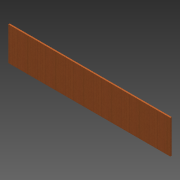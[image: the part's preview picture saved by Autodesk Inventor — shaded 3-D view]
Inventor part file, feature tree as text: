
AUTODESK INVENTOR PART (.ipt)
format: ipt  version: 2013 (Build 170138000, 138)  size: 80,896 bytes
history: native  units: in
note: dims shown in document units (in); Inventor stores cm internally (conversion verified against a paired STEP export)
features: extrude x1, sketch x1
ambient origin geometry x8: Origin, YZ Plane, XZ Plane, XY Plane, X Axis, Y Axis, Z Axis, Center Point
bodies: Solid1 (feature_tree)
feature tree (2):
  extrude  "Extrusion1"  Depth=12.0in
  sketch  "Sketch1"  dims[d0=58.0in d1=12.0in d2=0.5in d3=0.0in]
